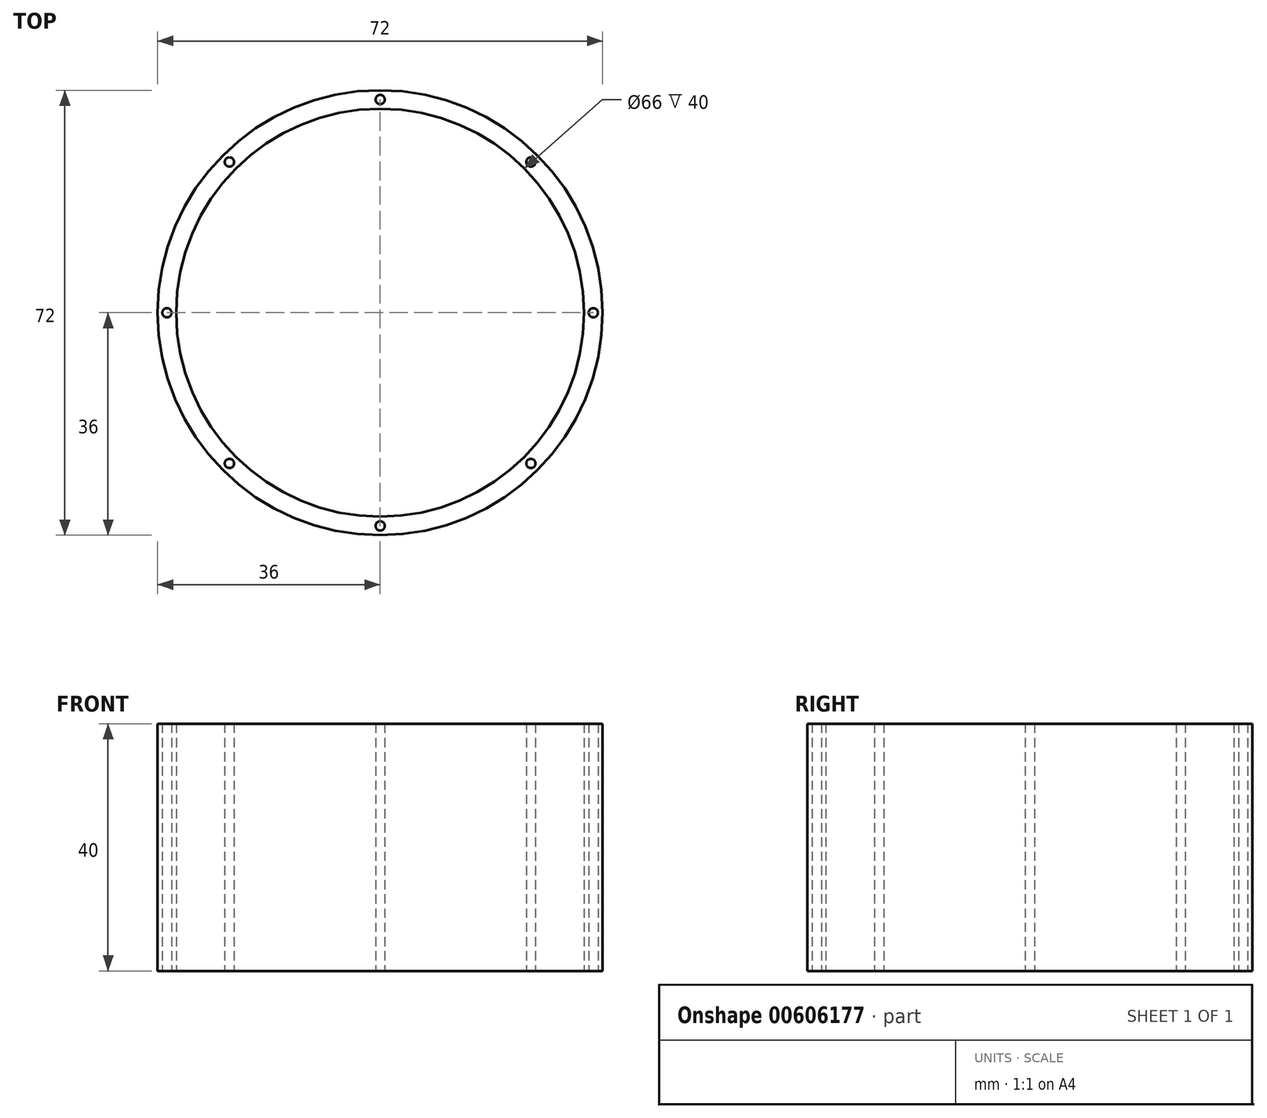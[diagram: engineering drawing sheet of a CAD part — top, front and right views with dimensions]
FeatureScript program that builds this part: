
annotation { "Feature Type Name" : "Feature", "Feature Type Description" : "" }
export const myFeature = defineFeature(function(context is Context, id is Id, definition is map)
    precondition{}
    {
        {
            var Q0;
            Q0=qCreatedBy(makeId("Top.planeOp"),FACE);
            var sketch = newSketch(context, id + "F0", { "sketchPlane" : qUnion([Q0])});
            skCircle(sketch, "E0", {"center": v(0, 0) * mm, "radius": 36 * mm});
            skSolve(sketch);
        }
        {
            var Q0;
            Q0 = qSketchRegion(id + "F0", true);
            extrude(context, id + "F1", {"entities" : qUnion([Q0]), "depth" : 40 * mm, "offsetDistance" : 25.4 * mm});
        }
        {
            var Q0;
            Q0=qCreatedBy(makeId("Top.planeOp"),FACE);
            var sketch = newSketch(context, id + "F2", { "sketchPlane" : qUnion([Q0])});
            skCircle(sketch, "E1", {"center": v(0, 0) * mm, "radius": 33 * mm});
            skSolve(sketch);
        }
        {
            var Q0;
            Q0=makeQuery(id+"F2.imprint","IMPRINT",FACE,{"disambiguationData":[TD([[makeQuery(id+"F2.imprint","IMPRINT",EDGE,{"derivedFrom":sQuery(id+"F2.wireOp",EDGE,"E1")}),1.0]])]});
            extrude(context, id + "F3", {"entities" : qUnion([Q0]), "operationType" : NewBodyOperationType.REMOVE, "endBound" : BoundingType.THROUGH_ALL, "depth" : 25.4 * mm, "offsetDistance" : 25.4 * mm});
        }
        {
            var Q0;
            Q0=qCreatedBy(makeId("Top.planeOp"),FACE);
            var sketch = newSketch(context, id + "F4", { "sketchPlane" : qUnion([Q0])});
            skCircle(sketch, "E2", {"center": v(0, 0) * mm, "radius": 34.5 * mm});
            skPoint(sketch, "E3", {"position": v(0, -34.5) * mm});
            skPoint(sketch, "E4.1.0", {"position": v(24.4, -24.4) * mm});
            skPoint(sketch, "E4.2.0", {"position": v(34.5, 0) * mm});
            skPoint(sketch, "E4.3.0", {"position": v(24.4, 24.4) * mm});
            skPoint(sketch, "E4.4.0", {"position": v(0, 34.5) * mm});
            skPoint(sketch, "E4.5.0", {"position": v(-24.4, 24.4) * mm});
            skPoint(sketch, "E4.6.0", {"position": v(-34.5, 0) * mm});
            skPoint(sketch, "E4.7.0", {"position": v(-24.4, -24.4) * mm});
            skSolve(sketch);
        }
        {
            var Q0;
            Q0=sQuery(id+"F4.wireOp",VERTEX,"E3");
            var Q1;
            Q1=sQuery(id+"F4.wireOp",VERTEX,"E4.7.0");
            var Q2;
            Q2=sQuery(id+"F4.wireOp",VERTEX,"E4.6.0");
            var Q3;
            Q3=sQuery(id+"F4.wireOp",VERTEX,"E4.1.0");
            var Q4;
            Q4=sQuery(id+"F4.wireOp",VERTEX,"E4.5.0");
            var Q5;
            Q5=sQuery(id+"F4.wireOp",VERTEX,"E4.4.0");
            var Q6;
            Q6=sQuery(id+"F4.wireOp",VERTEX,"E4.3.0");
            var Q7;
            Q7=sQuery(id+"F4.wireOp",VERTEX,"E4.2.0");
            var Q8;
            Q8=makeQuery(id+"F1.opExtrude","SWEPT_BODY",BODY,{"disambiguationData":[OSD([sQuery(id+"F0.wireOp",EDGE,"E0")])]});
            hole(context, id + "F5", {"style" : HoleStyle.SIMPLE, "endStyle" : HoleEndStyle.THROUGH, "oppositeDirection" : true, "standardTappedOrClearance" : lookupTablePath({ "standard" : "ISO", "size" : "1.5", "type" : "Drilled" }), "standardBlindInLast" : lookupTablePath({ "standard" : "ISO", "size" : "1.5", "type" : "Drilled" }), "holeDiameter" : 1.5 * mm, "majorDiameter" : 6.35 * mm, "tappedDepth" : 19.05 * mm, "tapClearance" : 3, "startFromSketch" : true, "locations" : qUnion([Q0, Q1, Q2, Q3, Q4, Q5, Q6, Q7]), "scope" : qUnion([Q8])});
        }
    });
